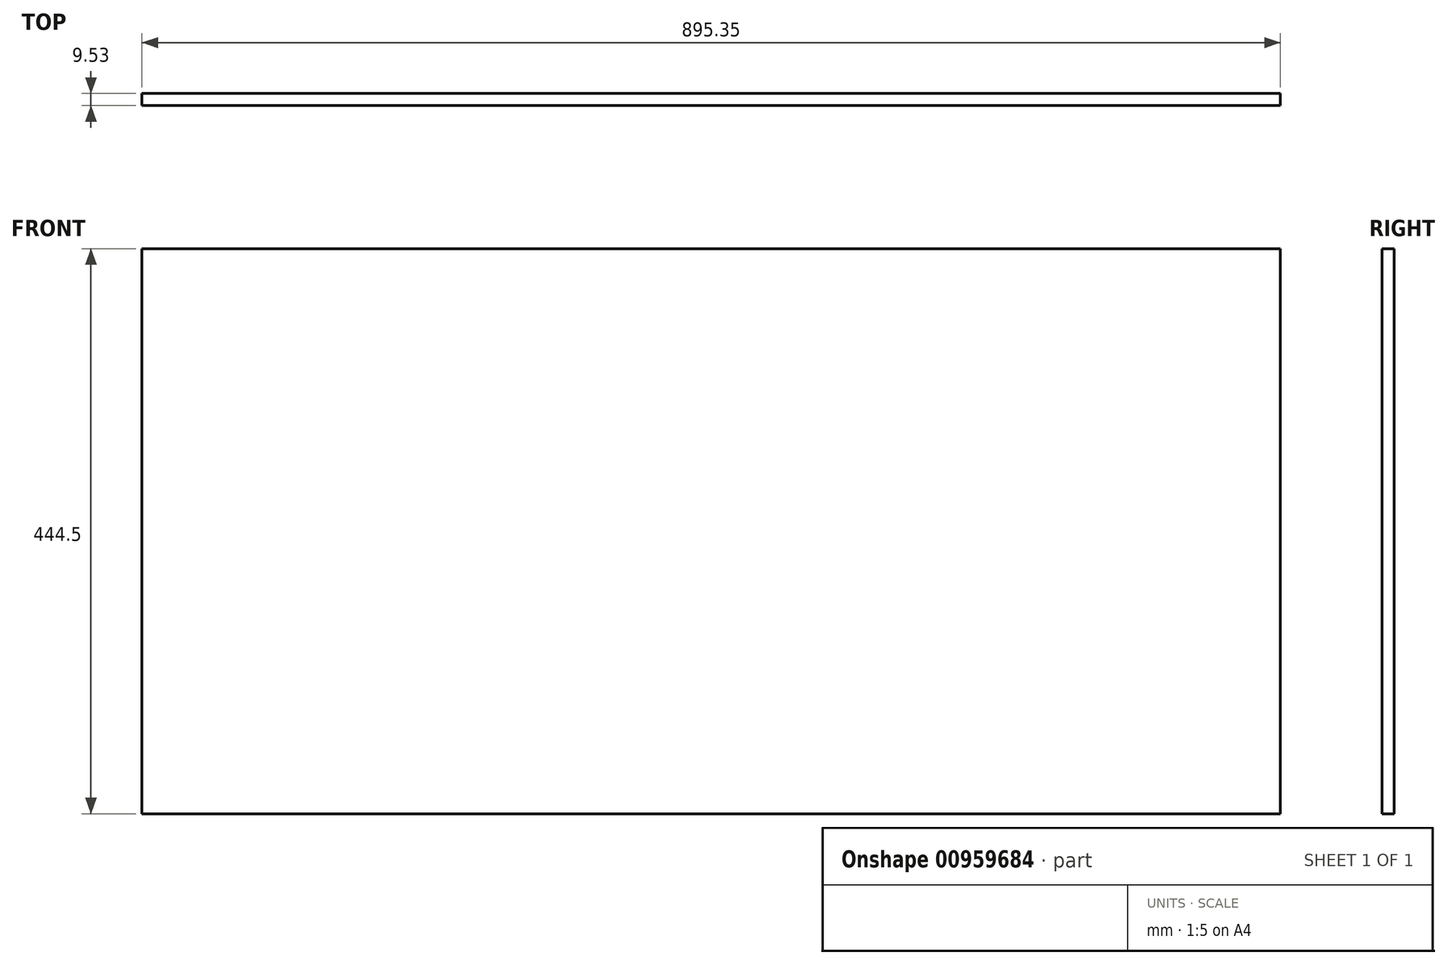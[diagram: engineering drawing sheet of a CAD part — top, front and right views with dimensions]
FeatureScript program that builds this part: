
annotation { "Feature Type Name" : "Feature", "Feature Type Description" : "" }
export const myFeature = defineFeature(function(context is Context, id is Id, definition is map)
    precondition{}
    {
        {
            var Q0;
            Q0=qCreatedBy(makeId("Front.planeOp"),FACE);
            var sketch = newSketch(context, id + "F0", { "sketchPlane" : qUnion([Q0])});
            skLineSegment(sketch, "E0.bottom", {"start": v(-621.3, 230.79) * mm, "end": v(274.04, 230.79) * mm});
            skLineSegment(sketch, "E0.top", {"start": v(-621.3, -213.71) * mm, "end": v(274.04, -213.71) * mm});
            skLineSegment(sketch, "E0.left", {"start": v(-621.3, 230.79) * mm, "end": v(-621.3, -213.71) * mm});
            skLineSegment(sketch, "E0.right", {"start": v(274.04, 230.79) * mm, "end": v(274.04, -213.71) * mm});
            skSolve(sketch);
        }
        {
            var Q0;
            Q0=makeQuery(id+"F0.imprint","IMPRINT",FACE,{"disambiguationData":[TD([[makeQuery(id+"F0.imprint","IMPRINT",EDGE,{"derivedFrom":sQuery(id+"F0.wireOp",EDGE,"E0.bottom")}),-1.0]])]});
            extrude(context, id + "F1", {"entities" : qUnion([Q0]), "depth" : 9.52 * mm, "offsetDistance" : 25.4 * mm});
        }
    });
